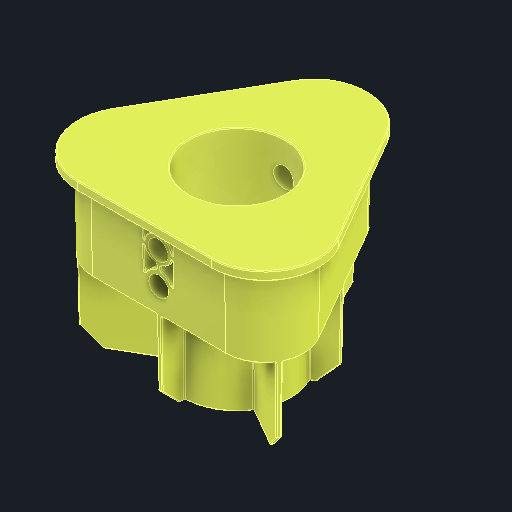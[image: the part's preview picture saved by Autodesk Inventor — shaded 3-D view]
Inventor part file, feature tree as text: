
AUTODESK INVENTOR PART (.ipt)
format: ipt  version: 2025 (Build 290162000, 162)  size: 1,731,584 bytes
history: native  units: in
note: dims shown in document units (in); Inventor stores cm internally (conversion verified against a paired STEP export)
features: fillet x1
ambient origin geometry x8: Origin, YZ Plane, XZ Plane, XY Plane, X Axis, Y Axis, Z Axis, Center Point
bodies: Solid1 (feature_tree)
feature tree (1):
  fillet  "Fillet45"  [1 undecoded]
note: 1 required parameter value undecoded (feature->parameter linkage not recoverable at this tier; creation-order binding heuristic only, values carry confidence <= 0.55)
